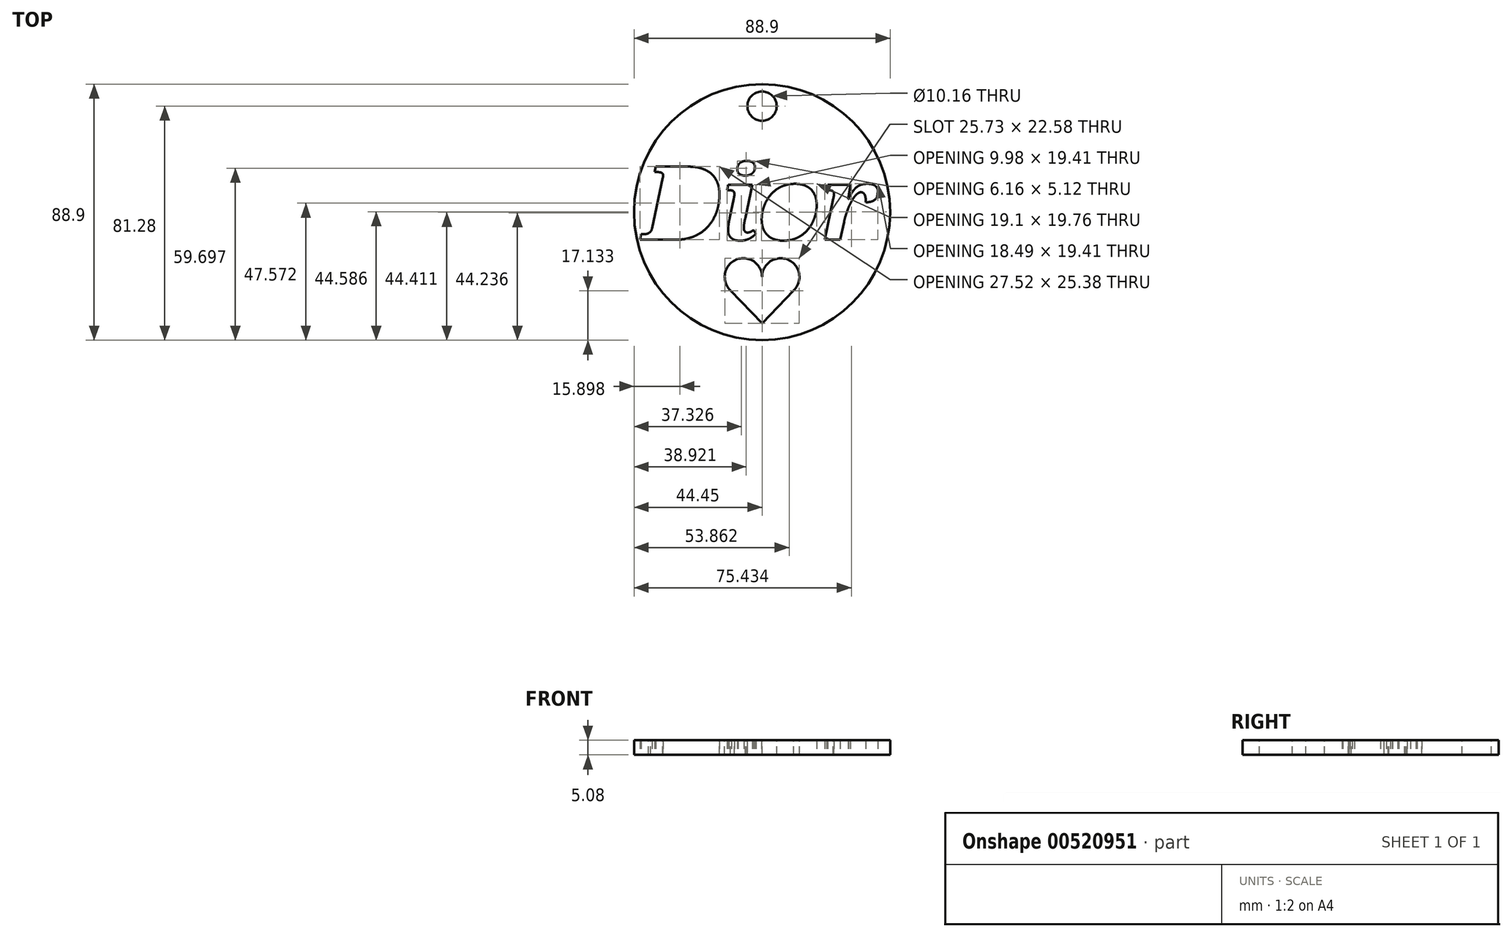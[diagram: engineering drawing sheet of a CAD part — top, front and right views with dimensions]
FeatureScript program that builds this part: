
annotation { "Feature Type Name" : "Feature", "Feature Type Description" : "" }
export const myFeature = defineFeature(function(context is Context, id is Id, definition is map)
    precondition{}
    {
        {
            var Q0;
            Q0=qCreatedBy(makeId("Top.planeOp"),FACE);
            var sketch = newSketch(context, id + "F0", { "sketchPlane" : qUnion([Q0])});
            skCircle(sketch, "E0", {"center": v(0, 0) * mm, "radius": 44.45 * mm});
            skText(sketch, "E1", { "text": "Dior", "fontName": "NotoSerif-BoldItalic.ttf"});
            const initialGuessF0  = {"E1": [-0.04146, -0.00957, 1, 0, 0.0256]};
            skSetInitialGuess(sketch, initialGuessF0);
            skSolve(sketch);
        }
        {
            var Q0;
            Q0=makeQuery(id+"F0.imprint","IMPRINT",FACE,{"disambiguationData":[TD([[makeQuery(id+"F0.imprint","IMPRINT",EDGE,{"derivedFrom":sQuery(id+"F0.wireOp",EDGE,"E0")}),1.0]])]});
            extrude(context, id + "F1", {"entities" : qUnion([Q0]), "depth" : 5.08 * mm, "offsetDistance" : 25.4 * mm});
        }
        {
            var Q0;
            Q0=makeQuery(id+"F1.opExtrude","CAP_FACE",FACE,{"disambiguationData":[OSD([sQuery(id+"F0.wireOp",EDGE,"E0"),sQuery(id+"F0.wireOp",EDGE,"E1.sketch_text.stroke-0"),sQuery(id+"F0.wireOp",EDGE,"E1.sketch_text.stroke-1"),sQuery(id+"F0.wireOp",EDGE,"E1.sketch_text.stroke-2"),sQuery(id+"F0.wireOp",EDGE,"E1.sketch_text.stroke-3"),sQuery(id+"F0.wireOp",EDGE,"E1.sketch_text.stroke-4"),sQuery(id+"F0.wireOp",EDGE,"E1.sketch_text.stroke-10"),sQuery(id+"F0.wireOp",EDGE,"E1.sketch_text.stroke-11"),sQuery(id+"F0.wireOp",EDGE,"E1.sketch_text.stroke-12"),sQuery(id+"F0.wireOp",EDGE,"E1.sketch_text.stroke-13"),sQuery(id+"F0.wireOp",EDGE,"E1.sketch_text.stroke-14"),sQuery(id+"F0.wireOp",EDGE,"E1.sketch_text.stroke-15"),sQuery(id+"F0.wireOp",EDGE,"E1.sketch_text.stroke-16"),sQuery(id+"F0.wireOp",EDGE,"E1.sketch_text.stroke-17"),sQuery(id+"F0.wireOp",EDGE,"E1.sketch_text.stroke-18"),sQuery(id+"F0.wireOp",EDGE,"E1.sketch_text.stroke-19"),sQuery(id+"F0.wireOp",EDGE,"E1.sketch_text.stroke-20"),sQuery(id+"F0.wireOp",EDGE,"E1.sketch_text.stroke-21"),sQuery(id+"F0.wireOp",EDGE,"E1.sketch_text.stroke-26"),sQuery(id+"F0.wireOp",EDGE,"E1.sketch_text.stroke-27"),sQuery(id+"F0.wireOp",EDGE,"E1.sketch_text.stroke-28"),sQuery(id+"F0.wireOp",EDGE,"E1.sketch_text.stroke-29"),sQuery(id+"F0.wireOp",EDGE,"E1.sketch_text.stroke-30"),sQuery(id+"F0.wireOp",EDGE,"E1.sketch_text.stroke-31"),sQuery(id+"F0.wireOp",EDGE,"E1.sketch_text.stroke-32"),sQuery(id+"F0.wireOp",EDGE,"E1.sketch_text.stroke-33"),sQuery(id+"F0.wireOp",EDGE,"E1.sketch_text.stroke-34"),sQuery(id+"F0.wireOp",EDGE,"E1.sketch_text.stroke-35"),sQuery(id+"F0.wireOp",EDGE,"E1.sketch_text.stroke-36")])],"isStart":false});
            var sketch = newSketch(context, id + "F2", { "sketchPlane" : qUnion([Q0])});
            skCircle(sketch, "E2", {"center": v(0, 12.89) * mm, "radius": 2.54 * mm});
            skSolve(sketch);
        }
        {
            var Q0;
            Q0=makeQuery(id+"F2.imprint","IMPRINT",FACE,{"disambiguationData":[TD([[makeQuery(id+"F2.imprint","IMPRINT",EDGE,{"derivedFrom":sQuery(id+"F2.wireOp",EDGE,"E2")}),-1.0]])]});
            var sketch = newSketch(context, id + "F3", { "sketchPlane" : qUnion([Q0])});
            skCircle(sketch, "E3", {"center": v(0, 36.83) * mm, "radius": 5.08 * mm});
            skSolve(sketch);
        }
        {
            var Q0;
            Q0=makeQuery(id+"F3.imprint","IMPRINT",FACE,{"disambiguationData":[TD([[makeQuery(id+"F3.imprint","IMPRINT",EDGE,{"derivedFrom":sQuery(id+"F3.wireOp",EDGE,"E3")}),1.0]])]});
            extrude(context, id + "F4", {"entities" : qUnion([Q0]), "operationType" : NewBodyOperationType.REMOVE, "oppositeDirection" : true, "depth" : 25.4 * mm, "offsetDistance" : 25.4 * mm});
        }
        {
            var Q0;
            Q0=makeQuery(id+"F1.opExtrude","CAP_FACE",FACE,{"disambiguationData":[OSD([sQuery(id+"F0.wireOp",EDGE,"E0"),sQuery(id+"F0.wireOp",EDGE,"E1.sketch_text.stroke-0"),sQuery(id+"F0.wireOp",EDGE,"E1.sketch_text.stroke-1"),sQuery(id+"F0.wireOp",EDGE,"E1.sketch_text.stroke-2"),sQuery(id+"F0.wireOp",EDGE,"E1.sketch_text.stroke-3"),sQuery(id+"F0.wireOp",EDGE,"E1.sketch_text.stroke-4"),sQuery(id+"F0.wireOp",EDGE,"E1.sketch_text.stroke-5"),sQuery(id+"F0.wireOp",EDGE,"E1.sketch_text.stroke-6"),sQuery(id+"F0.wireOp",EDGE,"E1.sketch_text.stroke-7"),sQuery(id+"F0.wireOp",EDGE,"E1.sketch_text.stroke-8"),sQuery(id+"F0.wireOp",EDGE,"E1.sketch_text.stroke-9"),sQuery(id+"F0.wireOp",EDGE,"E1.sketch_text.stroke-10"),sQuery(id+"F0.wireOp",EDGE,"E1.sketch_text.stroke-11"),sQuery(id+"F0.wireOp",EDGE,"E1.sketch_text.stroke-12"),sQuery(id+"F0.wireOp",EDGE,"E1.sketch_text.stroke-13"),sQuery(id+"F0.wireOp",EDGE,"E1.sketch_text.stroke-14"),sQuery(id+"F0.wireOp",EDGE,"E1.sketch_text.stroke-15"),sQuery(id+"F0.wireOp",EDGE,"E1.sketch_text.stroke-16"),sQuery(id+"F0.wireOp",EDGE,"E1.sketch_text.stroke-17"),sQuery(id+"F0.wireOp",EDGE,"E1.sketch_text.stroke-18"),sQuery(id+"F0.wireOp",EDGE,"E1.sketch_text.stroke-19"),sQuery(id+"F0.wireOp",EDGE,"E1.sketch_text.stroke-20"),sQuery(id+"F0.wireOp",EDGE,"E1.sketch_text.stroke-21"),sQuery(id+"F0.wireOp",EDGE,"E1.sketch_text.stroke-22"),sQuery(id+"F0.wireOp",EDGE,"E1.sketch_text.stroke-23"),sQuery(id+"F0.wireOp",EDGE,"E1.sketch_text.stroke-24"),sQuery(id+"F0.wireOp",EDGE,"E1.sketch_text.stroke-25"),sQuery(id+"F0.wireOp",EDGE,"E1.sketch_text.stroke-26"),sQuery(id+"F0.wireOp",EDGE,"E1.sketch_text.stroke-38"),sQuery(id+"F0.wireOp",EDGE,"E1.sketch_text.stroke-39"),sQuery(id+"F0.wireOp",EDGE,"E1.sketch_text.stroke-40"),sQuery(id+"F0.wireOp",EDGE,"E1.sketch_text.stroke-41"),sQuery(id+"F0.wireOp",EDGE,"E1.sketch_text.stroke-42"),sQuery(id+"F0.wireOp",EDGE,"E1.sketch_text.stroke-43"),sQuery(id+"F0.wireOp",EDGE,"E1.sketch_text.stroke-44"),sQuery(id+"F0.wireOp",EDGE,"E1.sketch_text.stroke-45"),sQuery(id+"F0.wireOp",EDGE,"E1.sketch_text.stroke-46"),sQuery(id+"F0.wireOp",EDGE,"E1.sketch_text.stroke-47"),sQuery(id+"F0.wireOp",EDGE,"E1.sketch_text.stroke-48"),sQuery(id+"F0.wireOp",EDGE,"E1.sketch_text.stroke-49"),sQuery(id+"F0.wireOp",EDGE,"E1.sketch_text.stroke-50"),sQuery(id+"F0.wireOp",EDGE,"E1.sketch_text.stroke-51"),sQuery(id+"F0.wireOp",EDGE,"E1.sketch_text.stroke-52"),sQuery(id+"F0.wireOp",EDGE,"E1.sketch_text.stroke-53"),sQuery(id+"F0.wireOp",EDGE,"E1.sketch_text.stroke-54"),sQuery(id+"F0.wireOp",EDGE,"E1.sketch_text.stroke-55"),sQuery(id+"F0.wireOp",EDGE,"E1.sketch_text.stroke-56"),sQuery(id+"F0.wireOp",EDGE,"E1.sketch_text.stroke-57"),sQuery(id+"F0.wireOp",EDGE,"E1.sketch_text.stroke-58"),sQuery(id+"F0.wireOp",EDGE,"E1.sketch_text.stroke-59"),sQuery(id+"F0.wireOp",EDGE,"E1.sketch_text.stroke-60"),sQuery(id+"F0.wireOp",EDGE,"E1.sketch_text.stroke-61"),sQuery(id+"F0.wireOp",EDGE,"E1.sketch_text.stroke-62"),sQuery(id+"F0.wireOp",EDGE,"E1.sketch_text.stroke-63"),sQuery(id+"F0.wireOp",EDGE,"E1.sketch_text.stroke-64"),sQuery(id+"F0.wireOp",EDGE,"E1.sketch_text.stroke-65"),sQuery(id+"F0.wireOp",EDGE,"E1.sketch_text.stroke-66"),sQuery(id+"F0.wireOp",EDGE,"E1.sketch_text.stroke-67"),sQuery(id+"F0.wireOp",EDGE,"E1.sketch_text.stroke-68"),sQuery(id+"F0.wireOp",EDGE,"E1.sketch_text.stroke-69"),sQuery(id+"F0.wireOp",EDGE,"E1.sketch_text.stroke-70"),sQuery(id+"F0.wireOp",EDGE,"E1.sketch_text.stroke-71"),sQuery(id+"F0.wireOp",EDGE,"E1.sketch_text.stroke-72"),sQuery(id+"F0.wireOp",EDGE,"E1.sketch_text.stroke-73"),sQuery(id+"F0.wireOp",EDGE,"E1.sketch_text.stroke-74"),sQuery(id+"F0.wireOp",EDGE,"E1.sketch_text.stroke-75"),sQuery(id+"F0.wireOp",EDGE,"E1.sketch_text.stroke-76"),sQuery(id+"F0.wireOp",EDGE,"E1.sketch_text.stroke-77"),sQuery(id+"F0.wireOp",EDGE,"E1.sketch_text.stroke-78"),sQuery(id+"F0.wireOp",EDGE,"E1.sketch_text.stroke-79"),sQuery(id+"F0.wireOp",EDGE,"E1.sketch_text.stroke-80"),sQuery(id+"F0.wireOp",EDGE,"E1.sketch_text.stroke-81"),sQuery(id+"F0.wireOp",EDGE,"E1.sketch_text.stroke-82"),sQuery(id+"F0.wireOp",EDGE,"E1.sketch_text.stroke-83"),sQuery(id+"F0.wireOp",EDGE,"E1.sketch_text.stroke-84"),sQuery(id+"F0.wireOp",EDGE,"E1.sketch_text.stroke-85"),sQuery(id+"F0.wireOp",EDGE,"E1.sketch_text.stroke-86"),sQuery(id+"F0.wireOp",EDGE,"E1.sketch_text.stroke-87"),sQuery(id+"F0.wireOp",EDGE,"E1.sketch_text.stroke-88"),sQuery(id+"F0.wireOp",EDGE,"E1.sketch_text.stroke-89"),sQuery(id+"F0.wireOp",EDGE,"E1.sketch_text.stroke-90"),sQuery(id+"F0.wireOp",EDGE,"E1.sketch_text.stroke-91"),sQuery(id+"F0.wireOp",EDGE,"E1.sketch_text.stroke-92"),sQuery(id+"F0.wireOp",EDGE,"E1.sketch_text.stroke-93"),sQuery(id+"F0.wireOp",EDGE,"E1.sketch_text.stroke-94"),sQuery(id+"F0.wireOp",EDGE,"E1.sketch_text.stroke-95"),sQuery(id+"F0.wireOp",EDGE,"E1.sketch_text.stroke-96"),sQuery(id+"F0.wireOp",EDGE,"E1.sketch_text.stroke-97"),sQuery(id+"F0.wireOp",EDGE,"E1.sketch_text.stroke-98"),sQuery(id+"F0.wireOp",EDGE,"E1.sketch_text.stroke-99"),sQuery(id+"F0.wireOp",EDGE,"E1.sketch_text.stroke-100"),sQuery(id+"F0.wireOp",EDGE,"E1.sketch_text.stroke-101"),sQuery(id+"F0.wireOp",EDGE,"E1.sketch_text.stroke-118"),sQuery(id+"F0.wireOp",EDGE,"E1.sketch_text.stroke-119"),sQuery(id+"F0.wireOp",EDGE,"E1.sketch_text.stroke-120"),sQuery(id+"F0.wireOp",EDGE,"E1.sketch_text.stroke-121"),sQuery(id+"F0.wireOp",EDGE,"E1.sketch_text.stroke-122"),sQuery(id+"F0.wireOp",EDGE,"E1.sketch_text.stroke-123"),sQuery(id+"F0.wireOp",EDGE,"E1.sketch_text.stroke-124"),sQuery(id+"F0.wireOp",EDGE,"E1.sketch_text.stroke-125"),sQuery(id+"F0.wireOp",EDGE,"E1.sketch_text.stroke-126"),sQuery(id+"F0.wireOp",EDGE,"E1.sketch_text.stroke-127"),sQuery(id+"F0.wireOp",EDGE,"E1.sketch_text.stroke-128"),sQuery(id+"F0.wireOp",EDGE,"E1.sketch_text.stroke-129"),sQuery(id+"F0.wireOp",EDGE,"E1.sketch_text.stroke-130"),sQuery(id+"F0.wireOp",EDGE,"E1.sketch_text.stroke-131"),sQuery(id+"F0.wireOp",EDGE,"E1.sketch_text.stroke-132"),sQuery(id+"F0.wireOp",EDGE,"E1.sketch_text.stroke-133"),sQuery(id+"F0.wireOp",EDGE,"E1.sketch_text.stroke-134"),sQuery(id+"F0.wireOp",EDGE,"E1.sketch_text.stroke-135"),sQuery(id+"F0.wireOp",EDGE,"E1.sketch_text.stroke-136"),sQuery(id+"F0.wireOp",EDGE,"E1.sketch_text.stroke-137"),sQuery(id+"F0.wireOp",EDGE,"E1.sketch_text.stroke-138"),sQuery(id+"F0.wireOp",EDGE,"E1.sketch_text.stroke-139"),sQuery(id+"F0.wireOp",EDGE,"E1.sketch_text.stroke-140"),sQuery(id+"F0.wireOp",EDGE,"E1.sketch_text.stroke-141"),sQuery(id+"F0.wireOp",EDGE,"E1.sketch_text.stroke-142"),sQuery(id+"F0.wireOp",EDGE,"E1.sketch_text.stroke-143"),sQuery(id+"F0.wireOp",EDGE,"E1.sketch_text.stroke-144"),sQuery(id+"F0.wireOp",EDGE,"E1.sketch_text.stroke-145"),sQuery(id+"F0.wireOp",EDGE,"E1.sketch_text.stroke-146"),sQuery(id+"F0.wireOp",EDGE,"E1.sketch_text.stroke-147")])],"isStart":false});
            var sketch = newSketch(context, id + "F5", { "sketchPlane" : qUnion([Q0])});
            skCircle(sketch, "E4", {"center": v(6.48, -22.49) * mm, "radius": 6.48 * mm});
            skCircle(sketch, "E5.MirrorC", {"center": v(-6.48, -22.49) * mm, "radius": 6.48 * mm});
            skLineSegment(sketch, "E6", {"start": v(-10.96, -27.17) * mm, "end": v(0, -38.6) * mm});
            skLineSegment(sketch, "E7.MirrorCS", {"start": v(10.96, -27.17) * mm, "end": v(0, -38.6) * mm});
            skSolve(sketch);
        }
        {
            var Q0;
            Q0 = qSketchRegion(id + "F5", true);
            extrude(context, id + "F6", {"entities" : qUnion([Q0]), "operationType" : NewBodyOperationType.REMOVE, "oppositeDirection" : true, "depth" : 25.4 * mm, "offsetDistance" : 25.4 * mm});
        }
    });
